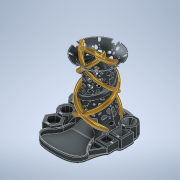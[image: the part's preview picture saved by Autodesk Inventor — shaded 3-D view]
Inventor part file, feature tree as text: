
AUTODESK INVENTOR PART (.ipt)
format: ipt  version: 2022 (Build 260153000, 153)  size: 8,123,904 bytes
history: native  units: mm
features: sketch x29, extrude x25, helix x5, fillet x4, plane x3, chamfer x3, revolve x2, pattern_circular x2
ambient origin geometry x8: Origin, YZ Plane, XZ Plane, XY Plane, X Axis, Y Axis, Z Axis, Center Point
bodies: Solid1 (feature_tree)
feature tree (73):
  revolve  "Revolution1"  [1 undecoded]
  plane  "Work Plane1"
  extrude  "Extrusion4"  Depth=20.0mm
  extrude  "Extrusion2"  Depth=19.0mm
  pattern_circular  "Circular Pattern2"  Count=9  [1 undecoded]
  plane  "Work Plane3"
  extrude  "Extrusion3"  Depth=10.0mm
  pattern_circular  "Circular Pattern3"  Count=7  [1 undecoded]
  helix  "Coil1"  [1 undecoded]
  helix  "Coil2"  [1 undecoded]
  helix  "Coil3"  [1 undecoded]
  helix  "Coil4"  [1 undecoded]
  helix  "Coil5"  [1 undecoded]
  extrude  "Extrusion5"  Depth=20.0mm
  revolve  "Revolution2"  [1 undecoded]
  extrude  "Extrusion6"  Depth=30.0mm
  extrude  "Extrusion7"  Depth=15.0mm
  extrude  "Extrusion15"  Depth=30.0mm
  extrude  "Extrusion16"  Depth=45.0mm
  extrude  "Extrusion17"  Depth=13.0mm
  extrude  "Extrusion18"  Depth=39.0mm
  extrude  "Extrusion19"  Depth=11.0mm
  extrude  "Extrusion20"  Depth=10.0mm
  extrude  "Extrusion21"  Depth=11.0mm
  extrude  "Extrusion22"  Depth=9.0mm
  extrude  "Extrusion23"  Depth=3.0mm TaperAngle=0.0deg
  extrude  "Extrusion25"  Depth=43.0mm
  extrude  "Extrusion26"  Depth=34.0mm
  extrude  "Extrusion27"  Depth=54.0mm TaperAngle=0.0deg
  extrude  "Extrusion28"  Depth=35.0mm
  extrude  "Extrusion29"  Depth=30.0mm
  extrude  "Extrusion30"  Depth=30.0mm
  extrude  "Extrusion31"  Depth=35.0mm
  extrude  "Extrusion32"  Depth=35.0mm
  chamfer  "Chamfer1"  Distance=5.0mm
  extrude  "Extrusion33"  Depth=10.0mm TaperAngle=0.0deg
  chamfer  "Chamfer2"  Distance=5.0mm
  chamfer  "Chamfer3"  Distance=10.0mm
  fillet  "Fillet4"  Radius=15.0mm
  fillet  "Fillet5"  Radius=0.2mm
  fillet  "Fillet6"  Radius=5.0mm
  extrude  "Extrusion34"  Depth=10.0mm TaperAngle=0.0deg
  fillet  "Fillet16"  Radius=15.0mm
  sketch  "Sketch1"  dims[d11=62.0mm d12=50.0mm]
  sketch  "Sketch3"  dims[d13=20.0mm d14=20.0mm]
  plane  "Work Plane2"
  sketch  "Sketch4"  dims[d15=23.0mm d16=19.0mm d17=90.0mm]
  sketch  "Sketch5"  dims[d18=32.0mm d19=10.0mm]
  sketch  "Sketch7"  dims[d20=151.0mm]
  sketch  "Sketch8"  dims[d26=2.0mm]
  sketch  "Sketch9"  dims[d27=2.0mm]
  sketch  "Sketch10"  dims[d28=2.0mm]
  sketch  "Sketch11"  dims[d29=2.0mm]
  sketch  "Sketch13"  dims[d30=2.0mm]
  sketch  "Sketch16"  dims[d31=90.0deg d32=70.0mm d38=77.75mm d39=0.0mm d40=40.0mm d41=360.0deg d43=70.0mm d44=77.75mm d45=0.0mm d46=40.0mm d47=360.0deg]
  sketch  "Sketch17"  dims[d49=20.0mm d50=20.0mm]
  sketch  "Sketch20"  dims[d51=20.0mm d52=20.0mm]
  sketch  "Sketch21"  dims[d53=40.0mm d54=30.0mm]
  sketch  "Sketch22"  dims[d55=30.0mm d56=15.0mm]
  sketch  "Sketch23"  dims[d57=15.0mm d58=30.0mm]
  sketch  "Sketch26"  dims[d59=77.75mm d60=0.0mm d61=45.0mm]
  sketch  "Sketch27"  dims[d62=35.0mm]
  sketch  "Sketch28"  dims[d63=70.0mm d64=100.0mm d65=10.0mm d66=-0.567232mm d67=90.0deg d68=90.0deg d69=90.0deg d70=90.0deg d71=13.0mm]
  sketch  "Sketch30"  dims[d72=10.0mm d73=39.0mm]
  sketch  "Sketch31"  dims[d74=140.0mm d75=160.0mm d76=10.0mm d77=-0.645772mm d78=90.0deg d79=90.0deg d80=90.0deg d81=90.0deg d82=11.0mm]
  sketch  "Sketch33"  dims[d83=39.0mm d84=10.0mm]
  sketch  "Sketch35"  dims[d85=135.0mm d86=160.0mm d87=10.0mm d88=-0.645772mm d89=90.0deg d90=90.0deg d91=90.0deg d92=90.0deg d93=11.0mm]
  sketch  "Sketch37"  dims[d94=170.0mm d95=160.0mm d96=10.0mm d97=-0.645772mm d98=90.0deg d99=90.0deg d100=90.0deg d101=90.0deg d102=9.0mm]
  sketch  "Sketch38"  dims[d103=170.0mm d104=160.0mm d105=10.0mm d106=-0.645772mm d107=90.0deg d108=90.0deg d109=90.0deg d110=90.0deg d125=3.0mm d126=0.0mm]
  sketch  "Sketch39"  dims[d128=60.0mm d129=43.0mm]
  sketch  "Sketch40"  dims[d130=270.0deg d132=34.0mm]
  sketch  "Sketch41"  dims[d133=54.0mm d134=0.0mm d136=54.0mm d137=0.0mm]
  sketch  "Sketch43"  dims[d141=35.0mm d165=35.0mm d166=30.0mm d167=30.0mm d168=30.0mm d169=30.0mm d170=35.0mm d172=35.0mm d186=5.0mm d187=10.0mm d188=0.0mm d190=5.0mm d191=0.0mm d192=10.0mm d193=0.0mm d194=15.0mm d195=0.0mm d196=0.2mm d197=0.0mm d198=5.0mm d199=0.0mm d200=10.0mm d201=0.0mm d202=15.0mm d203=0.0mm d204=3.0mm d205=0.0mm d210=1.0mm d211=0.0mm d213=10.0mm d214=0.0mm d215=20.0mm d216=24.0mm d217=20.0mm d218=30.0mm d219=23.5mm d220=5.75mm d221=5.75mm d222=5.75mm d223=14.0mm d224=0.0mm d225=22.5mm d226=6.25mm d227=6.25mm d228=6.25mm d229=14.0mm d230=0.0mm d231=25.0mm d232=5.0mm d233=5.0mm d234=5.0mm d235=14.0mm d236=0.0mm d237=25.5mm d239=3.0mm d241=10.0mm d242=0.0mm d243=54.0mm d244=43.0mm d245=17.5mm d246=17.5mm d247=7.0mm d248=5.5mm d249=4.0mm d250=3.607976mm d251=10.0mm d252=0.0mm d253=21.0mm d254=21.0mm d255=5.0mm d256=4.0mm d257=5.0mm d258=24.0mm d259=0.0mm d260=10.0mm d261=2.0mm d262=45.0deg d263=25.0mm d266=5.0mm d267=5.0mm d268=12.0mm d269=0.0mm d270=11.0mm d271=2.0mm d272=45.0deg d273=12.0mm d274=2.0mm d275=45.0deg d276=35.0mm d277=3.0mm d278=5.0mm d279=5.0mm d280=5.0mm d281=2.0mm d282=2.0mm d283=1.56mm d292=20.0mm d293=0.0mm d295=2.0mm d135=0.0mm]
note: 9 required parameter values undecoded (feature->parameter linkage not recoverable at this tier; creation-order binding heuristic only, values carry confidence <= 0.55)